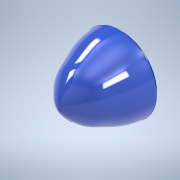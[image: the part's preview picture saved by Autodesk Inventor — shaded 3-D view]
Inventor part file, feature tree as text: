
AUTODESK INVENTOR PART (.ipt)
format: ipt  version: 2020 (Build 240168000, 168)  size: 219,136 bytes
history: native  units: mm
features: revolve x1, sketch x1
ambient origin geometry x8: Origin, YZ Plane, XZ Plane, XY Plane, X Axis, Y Axis, Z Axis, Center Point
bodies: Solid1 (feature_tree)
feature tree (2):
  revolve  "Revolution1"  [1 undecoded]
  sketch  "Sketch1"  dims[d21=90.0deg d25=2.0mm d26=2.0mm d27=2.0mm d29=10.0mm d31=29.0mm d32=48.0mm d33=25.0mm d34=15.0mm d35=27.0mm d11=0.872665mm d12=0.872665mm]
note: 1 required parameter value undecoded (feature->parameter linkage not recoverable at this tier; creation-order binding heuristic only, values carry confidence <= 0.55)
